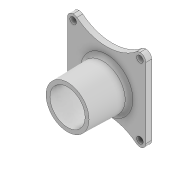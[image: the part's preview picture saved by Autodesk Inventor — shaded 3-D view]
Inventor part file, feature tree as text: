
AUTODESK INVENTOR PART (.ipt)
format: ipt  version: 2020 (Build 240168000, 168)  size: 216,064 bytes
history: native  units: mm
features: sketch x6, extrude x5, fillet x3, mirror x3, other x3, projected_geometry x2, revolve x1, reference x1
ambient origin geometry x8: Origin, YZ Plane, XZ Plane, XY Plane, X Axis, Y Axis, Z Axis, Center Point
bodies: Body1 (feature_tree)
feature tree (24):
  extrude  "Extrusion3"  Depth=42.0mm
  extrude  "Extrusion4"  Depth=3.0mm
  fillet  "Fillet2"  Radius=3.0mm
  mirror  "Mirror2"
  mirror  "Mirror3"
  extrude  "Extrusion5"  TaperAngle=0.0deg  [1 undecoded]
  mirror  "Mirror4"
  fillet  "Fillet3"  Radius=3.0mm
  extrude  "Extrusion6"  Depth=3.0mm TaperAngle=0.0deg
  extrude  "Extrusion7"  TaperAngle=0.0deg  [1 undecoded]
  revolve  "Revolution1"  [1 undecoded]
  fillet  "Fillet4"  Radius=20.0mm
  sketch  "Sketch3"  dims[d24=40.2mm d25=42.0mm]
  sketch  "Sketch4"  dims[d26=3.0mm d27=0.0mm d28=3.0mm d29=3.0mm]
  sketch  "Sketch5"  dims[d30=3.4mm d31=0.0mm d32=0.0mm d33=3.0mm]
  sketch  "Sketch7"  dims[d34=3.0mm d35=1.5mm d36=0.0mm]
  reference  "Reference1"
  sketch  "Sketch8"  dims[d37=3.0mm d39=0.0mm d40=0.0mm]
  projected_geometry  "Projected Loop1"
  sketch  "Sketch9"  dims[d41=18.0mm d42=22.0mm d43=20.0mm d44=0.0mm d45=0.5mm d46=90.0deg d47=2.0mm d48=1.1mm d49=1.1mm]
  projected_geometry  "Projected Loop2"
  other  "<userpath>\Google Drive\Breathney\oxymount.iam"
  other  "oxymount.iam"
  other  "oxysens:1"
note: 3 required parameter values undecoded (feature->parameter linkage not recoverable at this tier; creation-order binding heuristic only, values carry confidence <= 0.55)